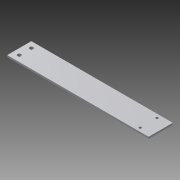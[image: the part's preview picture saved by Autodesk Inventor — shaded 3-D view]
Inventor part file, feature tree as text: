
AUTODESK INVENTOR PART (.ipt)
format: ipt  version: 2015 (Build 190159000, 159)  size: 118,272 bytes
history: native  units: mm
features: sketch x4, extrude x2, hole x2, other x1
ambient origin geometry x8: Origin, YZ Plane, XZ Plane, XY Plane, X Axis, Y Axis, Z Axis, Center Point
bodies: Body1 (feature_tree)
feature tree (9):
  other  "ソリッド1"
  extrude  "押し出し1"  Depth=112.0mm
  hole  "穴1"  [1 undecoded]
  hole  "穴3"  [1 undecoded]
  extrude  "押し出し3"  Depth=10.0mm
  sketch  "スケッチ1"
  sketch  "スケッチ3"
  sketch  "スケッチ5"
  sketch  "スケッチ6"
note: 2 required parameter values undecoded (feature->parameter linkage not recoverable at this tier; creation-order binding heuristic only, values carry confidence <= 0.55)
